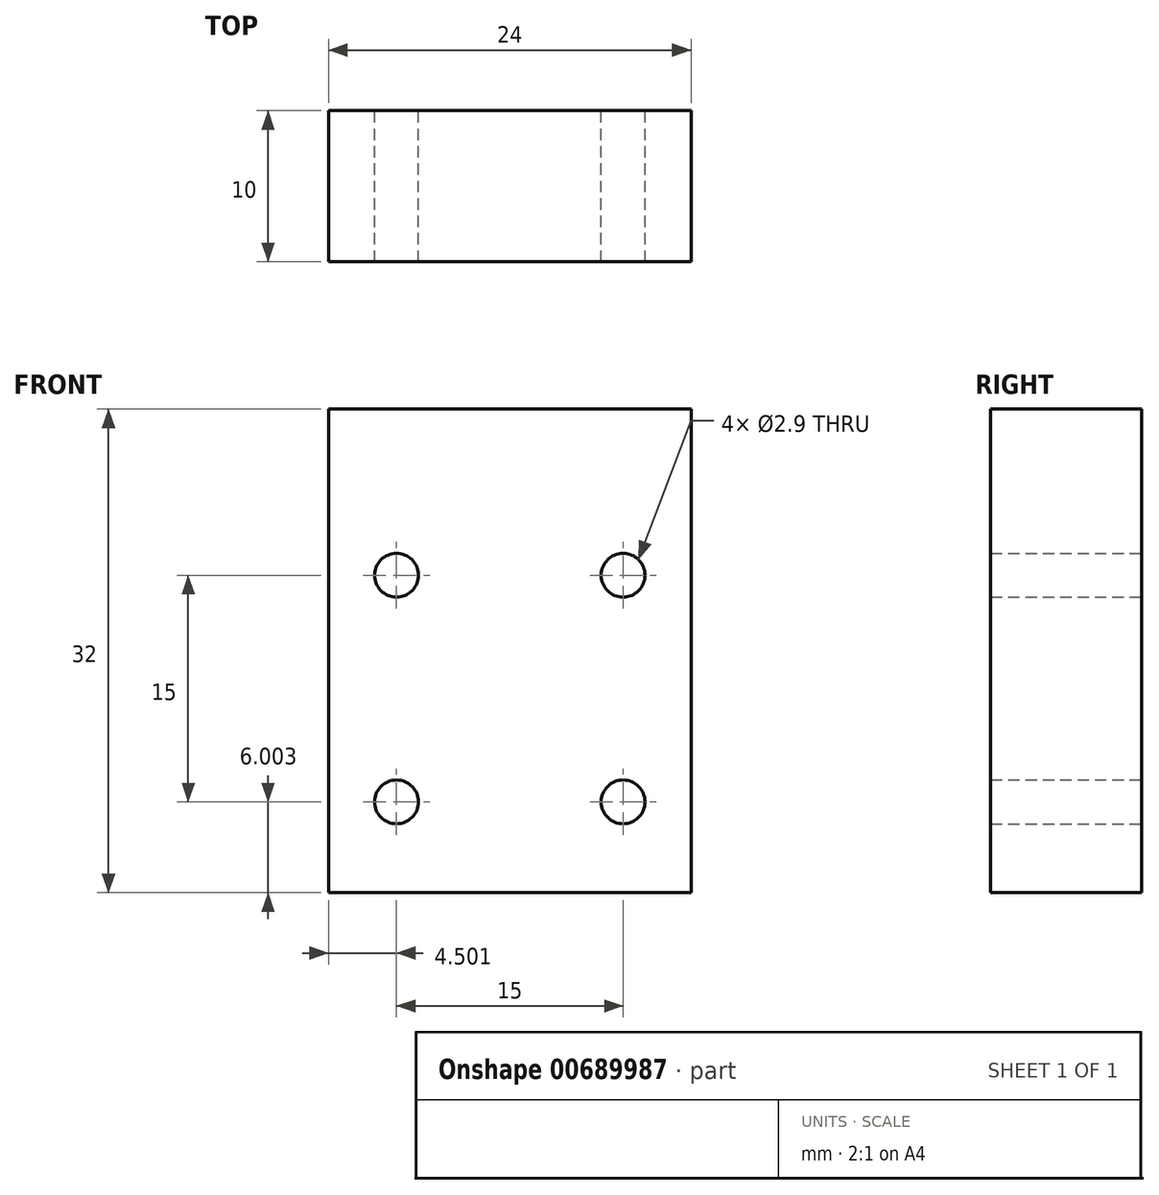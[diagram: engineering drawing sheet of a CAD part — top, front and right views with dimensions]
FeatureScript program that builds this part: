
annotation { "Feature Type Name" : "Feature", "Feature Type Description" : "" }
export const myFeature = defineFeature(function(context is Context, id is Id, definition is map)
    precondition{}
    {
        {
            var Q0;
            Q0=qCreatedBy(makeId("Front.planeOp"),FACE);
            var sketch = newSketch(context, id + "F0", { "sketchPlane" : qUnion([Q0])});
            skLineSegment(sketch, "E0.bottom", {"start": v(-24.47, 31.11) * mm, "end": v(-0.47, 31.11) * mm});
            skLineSegment(sketch, "E0.top", {"start": v(-24.47, -0.89) * mm, "end": v(-0.47, -0.89) * mm});
            skLineSegment(sketch, "E0.left", {"start": v(-24.47, 31.11) * mm, "end": v(-24.47, -0.89) * mm});
            skLineSegment(sketch, "E0.right", {"start": v(-0.47, 31.11) * mm, "end": v(-0.47, -0.89) * mm});
            skCircle(sketch, "E1", {"center": v(-19.97, 20.11) * mm, "radius": 1.45 * mm});
            skCircle(sketch, "E2", {"center": v(-4.97, 20.11) * mm, "radius": 1.45 * mm});
            skCircle(sketch, "E3", {"center": v(-19.97, 5.11) * mm, "radius": 1.45 * mm});
            skCircle(sketch, "E4", {"center": v(-4.97, 5.11) * mm, "radius": 1.45 * mm});
            skLineSegment(sketch, "E5", {"start": v(-19.97, 20.11) * mm, "end": v(-4.97, 20.11) * mm});
            skLineSegment(sketch, "E6", {"start": v(-4.97, 5.11) * mm, "end": v(-4.97, 20.11) * mm});
            skLineSegment(sketch, "E7", {"start": v(-19.97, 20.11) * mm, "end": v(-19.97, 5.11) * mm});
            skLineSegment(sketch, "E8", {"start": v(-19.97, 5.11) * mm, "end": v(-4.97, 5.11) * mm});
            skLineSegment(sketch, "E9", {"start": v(-19.97, 20.11) * mm, "end": v(-24.47, 20.11) * mm});
            skLineSegment(sketch, "E10", {"start": v(-0.47, 13.47) * mm, "end": v(-4.97, 13.47) * mm});
            skLineSegment(sketch, "E11", {"start": v(-12.47, 31.11) * mm, "end": v(-12.47, 20.11) * mm});
            skPoint(sketch, "E12.startSnap0", {"position": v(-19.97, 12.61) * mm});
            skSolve(sketch);
        }
        {
            var Q0;
            {var subQ0=sQuery(id+"F0.wireOp",EDGE,"E10");Q0=makeQuery(id+"F0.imprint","IMPRINT",FACE,{"disambiguationData":[TD([[makeQuery(id+"F0.imprint","IMPRINT",EDGE,{"derivedFrom":subQ0}),-1.0]])]});}
            var Q1;
            {var subQ5=sQuery(id+"F0.wireOp",EDGE,"E0.left");var subQ6=sQuery(id+"F0.wireOp",EDGE,"E0.bottom");var subQ7=makeQuery(id+"F0.imprint","INTERSECT",VERTEX,{"derivedFrom":[subQ6,subQ5]});Q1=makeQuery(id+"F0.imprint","IMPRINT",FACE,{"disambiguationData":[TD([[makeQuery(id+"F0.imprint","IMPRINT",EDGE,{"disambiguationData":[TD([[subQ7,-1.0]])],"derivedFrom":subQ6}),-1.0]])]});}
            var Q2;
            {var subQ9=sQuery(id+"F0.wireOp",EDGE,"E5");var subQ14=sQuery(id+"F0.wireOp",EDGE,"E1");var subQ15=makeQuery(id+"F0.imprint","INTERSECT",VERTEX,{"derivedFrom":[subQ14,subQ9]});Q2=makeQuery(id+"F0.imprint","IMPRINT",FACE,{"disambiguationData":[TD([[makeQuery(id+"F0.imprint","IMPRINT",EDGE,{"disambiguationData":[TD([[subQ15,1.0]])],"derivedFrom":subQ14}),-1.0]])]});}
            var Q3;
            {var subQ9=sQuery(id+"F0.wireOp",EDGE,"E0.top");var subQ11=sQuery(id+"F0.wireOp",EDGE,"E0.left");var subQ12=makeQuery(id+"F0.imprint","INTERSECT",VERTEX,{"derivedFrom":[subQ9,subQ11]});Q3=makeQuery(id+"F0.imprint","IMPRINT",FACE,{"disambiguationData":[TD([[makeQuery(id+"F0.imprint","IMPRINT",EDGE,{"disambiguationData":[TD([[subQ12,-1.0]])],"derivedFrom":subQ9}),1.0]])]});}
            var Q4;
            {var subQ5=sQuery(id+"F0.wireOp",EDGE,"E10");Q4=makeQuery(id+"F0.imprint","IMPRINT",FACE,{"disambiguationData":[TD([[makeQuery(id+"F0.imprint","IMPRINT",EDGE,{"derivedFrom":subQ5}),1.0]])]});}
            var Q5;
            {var subQ0=sQuery(id+"F0.wireOp",EDGE,"87J4U4OK-eTJd-vyFb-n9Ve-Y68HN9CrHsac");Q5=makeQuery(id+"F0.imprint","IMPRINT",FACE,{"disambiguationData":[TD([[makeQuery(id+"F0.imprint","IMPRINT",EDGE,{"derivedFrom":subQ0}),1.0]])]});}
            var Q6;
            {var subQ0=sQuery(id+"F0.wireOp",EDGE,"HUbwwHt9-QyLK-z4km-9Kyn-OP1rpeKwMXWI");Q6=makeQuery(id+"F0.imprint","IMPRINT",FACE,{"disambiguationData":[TD([[makeQuery(id+"F0.imprint","IMPRINT",EDGE,{"derivedFrom":subQ0}),-1.0]])]});}
            extrude(context, id + "F1", {"entities" : qUnion([Q0, Q1, Q2, Q3, Q4, Q5, Q6]), "depth" : 10 * mm, "offsetDistance" : 25 * mm});
        }
    });
